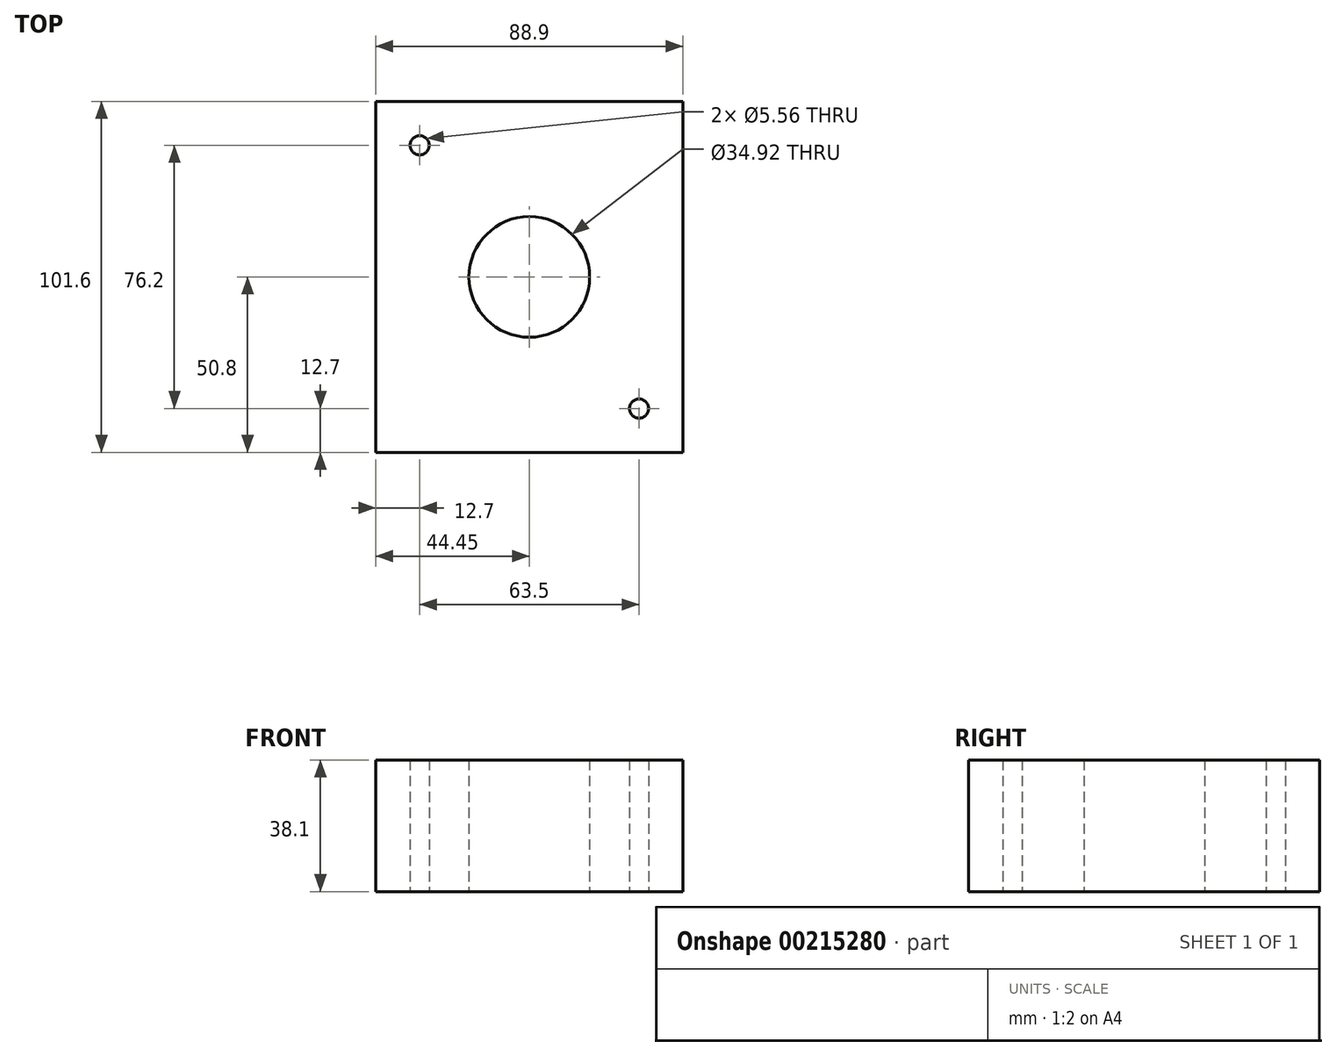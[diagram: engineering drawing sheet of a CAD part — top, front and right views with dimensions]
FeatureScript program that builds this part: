
annotation { "Feature Type Name" : "Feature", "Feature Type Description" : "" }
export const myFeature = defineFeature(function(context is Context, id is Id, definition is map)
    precondition{}
    {
        {
            var Q0;
            Q0=qCreatedBy(makeId("Top.planeOp"),FACE);
            var sketch = newSketch(context, id + "F0", { "sketchPlane" : qUnion([Q0])});
            skLineSegment(sketch, "E0.bottom", {"start": v(-44.45, 50.8) * mm, "end": v(44.45, 50.8) * mm});
            skLineSegment(sketch, "E0.top", {"start": v(-44.45, -50.8) * mm, "end": v(44.45, -50.8) * mm});
            skLineSegment(sketch, "E0.left", {"start": v(-44.45, 50.8) * mm, "end": v(-44.45, -50.8) * mm});
            skLineSegment(sketch, "E0.right", {"start": v(44.45, 50.8) * mm, "end": v(44.45, -50.8) * mm});
            skCircle(sketch, "E1", {"center": v(0, 0) * mm, "radius": 17.46 * mm});
            skCircle(sketch, "E2", {"center": v(-31.75, 38.1) * mm, "radius": 2.78 * mm});
            skCircle(sketch, "E3", {"center": v(31.75, -38.1) * mm, "radius": 2.78 * mm});
            skSolve(sketch);
        }
        {
            var Q0;
            Q0=makeQuery(id+"F0.imprint","IMPRINT",FACE,{"disambiguationData":[TD([[makeQuery(id+"F0.imprint","IMPRINT",EDGE,{"derivedFrom":sQuery(id+"F0.wireOp",EDGE,"E0.bottom")}),-1.0]])]});
            extrude(context, id + "F1", {"entities" : qUnion([Q0]), "depth" : 38.1 * mm});
        }
    });
